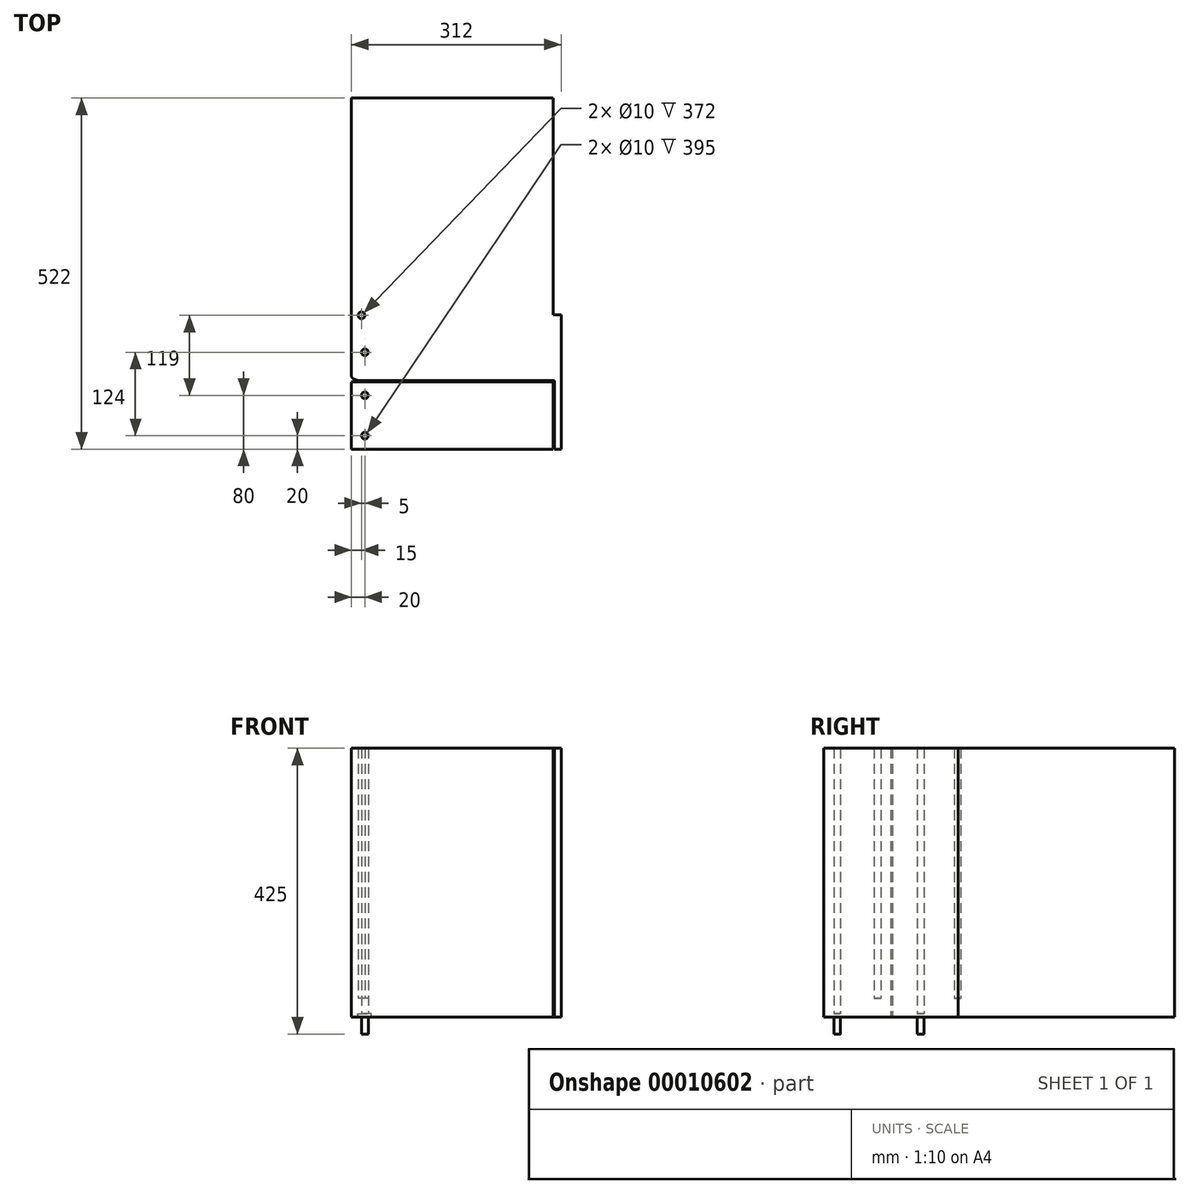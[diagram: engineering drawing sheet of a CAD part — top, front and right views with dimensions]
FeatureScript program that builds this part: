
annotation { "Feature Type Name" : "Feature", "Feature Type Description" : "" }
export const myFeature = defineFeature(function(context is Context, id is Id, definition is map)
    precondition{}
    {
        {
            var Q0;
            Q0=qCreatedBy(makeId("Top.planeOp"),FACE);
            var sketch = newSketch(context, id + "F0", { "sketchPlane" : qUnion([Q0])});
            skLineSegment(sketch, "E0.bottom", {"start": v(0, 420) * mm, "end": v(300, 420) * mm});
            skLineSegment(sketch, "E0.top", {"start": v(0, 0) * mm, "end": v(300, 0) * mm});
            skLineSegment(sketch, "E0.left", {"start": v(0, 420) * mm, "end": v(0, 0) * mm});
            skLineSegment(sketch, "E0.right", {"start": v(300, 420) * mm, "end": v(300, 0) * mm});
            skLineSegment(sketch, "E1.bottom", {"start": v(0, -2) * mm, "end": v(300, -2) * mm});
            skLineSegment(sketch, "E1.top", {"start": v(0, -102) * mm, "end": v(300, -102) * mm});
            skLineSegment(sketch, "E1.left", {"start": v(0, -2) * mm, "end": v(0, -102) * mm});
            skLineSegment(sketch, "E1.right", {"start": v(300, -2) * mm, "end": v(300, -102) * mm});
            skCircle(sketch, "E2", {"center": v(20, 42) * mm, "radius": 5 * mm});
            skCircle(sketch, "E3", {"center": v(15, 97) * mm, "radius": 5 * mm});
            skCircle(sketch, "E4", {"center": v(20, -22) * mm, "radius": 5 * mm});
            skCircle(sketch, "E5", {"center": v(20, -82) * mm, "radius": 5 * mm});
            skLineSegment(sketch, "E6.bottom", {"start": v(-62.26, -84.61) * mm, "end": v(209.63, -211.4) * mm, "construction": true});
            skLineSegment(sketch, "E6.top", {"start": v(-20, 6.02) * mm, "end": v(251.9, -120.77) * mm, "construction": true});
            skLineSegment(sketch, "E6.left", {"start": v(-20, 6.02) * mm, "end": v(-62.26, -84.61) * mm, "construction": true});
            skLineSegment(sketch, "E6.right", {"start": v(251.9, -120.77) * mm, "end": v(209.63, -211.4) * mm, "construction": true});
            skCircle(sketch, "E7", {"center": v(-10.33, -20.56) * mm, "radius": 5 * mm, "construction": true});
            skCircle(sketch, "E8", {"center": v(-35.68, -74.94) * mm, "radius": 5 * mm, "construction": true});
            skLineSegment(sketch, "E9", {"start": v(-35.68, -74.94) * mm, "end": v(20, -82) * mm, "construction": true});
            skLineSegment(sketch, "E10", {"start": v(-7.84, -78.47) * mm, "end": v(55.35, 420) * mm, "construction": true});
            skLineSegment(sketch, "E11", {"start": v(-10.33, -20.56) * mm, "end": v(20, -22) * mm, "construction": true});
            skLineSegment(sketch, "E12", {"start": v(4.84, -21.28) * mm, "end": v(25.75, 420) * mm, "construction": true});
            skLineSegment(sketch, "E13.bottom", {"start": v(302, -102) * mm, "end": v(312, -102) * mm});
            skLineSegment(sketch, "E13.top", {"start": v(302, 98) * mm, "end": v(312, 98) * mm});
            skLineSegment(sketch, "E13.left", {"start": v(302, -102) * mm, "end": v(302, 98) * mm});
            skLineSegment(sketch, "E13.right", {"start": v(312, -102) * mm, "end": v(312, 98) * mm});
            skLineSegment(sketch, "E14.bottom", {"start": v(302, 98) * mm, "end": v(300, 98) * mm});
            skLineSegment(sketch, "E14.top", {"start": v(302, 0) * mm, "end": v(300, 0) * mm});
            skLineSegment(sketch, "E14.left", {"start": v(302, 98) * mm, "end": v(302, 0) * mm});
            skLineSegment(sketch, "E14.right", {"start": v(300, 98) * mm, "end": v(300, 0) * mm});
            skSolve(sketch);
        }
        {
            var Q0;
            Q0 = qSketchRegion(id + "F0", true);
            extrude(context, id + "F1", {"entities" : qUnion([Q0]), "depth" : 400 * mm});
        }
        {
            var Q0;
            Q0=qCreatedBy(makeId("Top.planeOp"),FACE);
            var sketch = newSketch(context, id + "F2", { "sketchPlane" : qUnion([Q0])});
            skLineSegment(sketch, "E15", {"start": v(25, 97.42) * mm, "end": v(30, -21.58) * mm});
            skLineSegment(sketch, "E16", {"start": v(10, -22.42) * mm, "end": v(5, 96.58) * mm});
            skArc(sketch, "E17", {"start": v(5, 96.58) * mm, "mid": v(14.58, 107) * mm, "end": v(25, 97.42) * mm});
            skArc(sketch, "E18", {"start": v(30, -21.58) * mm, "mid": v(20.42, -32) * mm, "end": v(10, -22.42) * mm});
            skCircle(sketch, "E19", {"center": v(15, 97) * mm, "radius": 5 * mm});
            skCircle(sketch, "E20", {"center": v(20, -22) * mm, "radius": 5 * mm});
            skSolve(sketch);
        }
        {
            var Q0;
            {var subQ3=sQuery(id+"F2.wireOp",EDGE,"E16");Q0=makeQuery(id+"F2.imprint","IMPRINT",FACE,{"disambiguationData":[TD([[makeQuery(id+"F2.imprint","IMPRINT",EDGE,{"derivedFrom":subQ3}),-1.0]])]});}
            var Q1;
            {var subQ0=sQuery(id+"F2.wireOp",EDGE,"E18");var subQ1=sQuery(id+"F2.wireOp",EDGE,"1002cabe-0871-408c-8a85-3f84f857aeda");var subQ2=makeQuery(id+"F2.imprint","INTERSECT",VERTEX,{"derivedFrom":[subQ1,subQ0]});Q1=makeQuery(id+"F2.imprint","IMPRINT",FACE,{"disambiguationData":[TD([[makeQuery(id+"F2.imprint","IMPRINT",EDGE,{"disambiguationData":[TD([[subQ2,-1.0]])],"derivedFrom":subQ1}),-1.0]])]});}
            var Q2;
            Q2=makeQuery(id+"F2.imprint","IMPRINT",FACE,{"disambiguationData":[TD([[makeQuery(id+"F2.imprint","IMPRINT",EDGE,{"derivedFrom":sQuery(id+"F2.wireOp",EDGE,"E20")}),1.0]])]});
            var Q3;
            Q3=makeQuery(id+"F2.imprint","IMPRINT",FACE,{"disambiguationData":[TD([[makeQuery(id+"F2.imprint","IMPRINT",EDGE,{"derivedFrom":sQuery(id+"F2.wireOp",EDGE,"E19")}),1.0]])]});
            extrude(context, id + "F3", {"entities" : qUnion([Q0, Q1, Q2, Q3]), "depth" : 5 * mm});
        }
        {
            var Q0;
            Q0=makeQuery(id+"F2.imprint","IMPRINT",FACE,{"disambiguationData":[TD([[makeQuery(id+"F2.imprint","IMPRINT",EDGE,{"derivedFrom":sQuery(id+"F2.wireOp",EDGE,"E19")}),1.0]])]});
            var Q1;
            Q1=makeQuery(id+"F2.imprint","IMPRINT",FACE,{"disambiguationData":[TD([[makeQuery(id+"F2.imprint","IMPRINT",EDGE,{"derivedFrom":sQuery(id+"F2.wireOp",EDGE,"E20")}),1.0]])]});
            extrude(context, id + "F4", {"entities" : qUnion([Q0, Q1]), "operationType" : NewBodyOperationType.ADD, "depth" : 28 * mm});
        }
        {
            var Q0;
            Q0=qCreatedBy(makeId("Top.planeOp"),FACE);
            var sketch = newSketch(context, id + "F5", { "sketchPlane" : qUnion([Q0])});
            skLineSegment(sketch, "E21", {"start": v(30, 42) * mm, "end": v(30, -82) * mm});
            skLineSegment(sketch, "E22", {"start": v(10, -82) * mm, "end": v(10, 42) * mm});
            skArc(sketch, "E23", {"start": v(10, 42) * mm, "mid": v(20, 52) * mm, "end": v(30, 42) * mm});
            skArc(sketch, "E24", {"start": v(30, -82) * mm, "mid": v(20, -92) * mm, "end": v(10, -82) * mm});
            skCircle(sketch, "E25", {"center": v(20, 42) * mm, "radius": 5 * mm});
            skCircle(sketch, "E26", {"center": v(20, -82) * mm, "radius": 5 * mm});
            skSolve(sketch);
        }
        {
            var Q0;
            Q0=makeQuery(id+"F5.imprint","IMPRINT",FACE,{"disambiguationData":[TD([[makeQuery(id+"F5.imprint","IMPRINT",EDGE,{"derivedFrom":sQuery(id+"F5.wireOp",EDGE,"E21")}),-1.0]])]});
            var Q1;
            Q1=makeQuery(id+"F5.imprint","IMPRINT",FACE,{"disambiguationData":[TD([[makeQuery(id+"F5.imprint","IMPRINT",EDGE,{"derivedFrom":sQuery(id+"F5.wireOp",EDGE,"E25")}),1.0]])]});
            var Q2;
            Q2=makeQuery(id+"F5.imprint","IMPRINT",FACE,{"disambiguationData":[TD([[makeQuery(id+"F5.imprint","IMPRINT",EDGE,{"derivedFrom":sQuery(id+"F5.wireOp",EDGE,"E26")}),1.0]])]});
            extrude(context, id + "F6", {"entities" : qUnion([Q0, Q1, Q2]), "depth" : 5 * mm});
        }
        {
            var Q0;
            Q0=makeQuery(id+"F5.imprint","IMPRINT",FACE,{"disambiguationData":[TD([[makeQuery(id+"F5.imprint","IMPRINT",EDGE,{"derivedFrom":sQuery(id+"F5.wireOp",EDGE,"E26")}),1.0]])]});
            var Q1;
            Q1=makeQuery(id+"F5.imprint","IMPRINT",FACE,{"disambiguationData":[TD([[makeQuery(id+"F5.imprint","IMPRINT",EDGE,{"derivedFrom":sQuery(id+"F5.wireOp",EDGE,"E25")}),1.0]])]});
            var Q2;
            Q2=sQuery(id+"F2.wireOp",EDGE,"E19");
            var Q3;
            Q3=sQuery(id+"F2.wireOp",EDGE,"E20");
            extrude(context, id + "F7", {"entities" : qUnion([Q0, Q1]), "operationType" : NewBodyOperationType.ADD, "surfaceEntities" : qUnion([Q2, Q3]), "oppositeDirection" : true, "depth" : 25 * mm});
        }
        {
            var Q0;
            Q0=makeQuery(id+"F1.opExtrude","SWEPT_EDGE",EDGE,{"disambiguationData":[OSD([sQuery(id+"F0.wireOp",EDGE,"E0.top"),sQuery(id+"F0.wireOp",EDGE,"E0.left")])]});
            chamfer(context, id + "F8", {"entities" : qUnion([Q0]), "chamferType" : ChamferType.TWO_OFFSETS, "width1" : 9 * mm, "oppositeDirection" : false, "width2" : 4 * mm});
        }
        {
            var Q0;
            Q0=makeQuery(id+"F1.opExtrude","SWEPT_EDGE",EDGE,{"disambiguationData":[OSD([sQuery(id+"F0.wireOp",EDGE,"E0.top"),sQuery(id+"F0.wireOp",EDGE,"E0.left")])]});
            var Q1;
            {var subQ0=sQuery(id+"F0.wireOp",EDGE,"E0.left");Q1=makeQuery(id+"F8.opChamfer","BLEND_EDGE",EDGE,{"blendedFrom":[makeQuery(id+"F1.opExtrude","SWEPT_EDGE",EDGE,{"disambiguationData":[OSD([sQuery(id+"F0.wireOp",EDGE,"E0.top"),subQ0])]}),makeQuery(id+"F1.opExtrude","SWEPT_FACE",FACE,{"disambiguationData":[OSD([subQ0])]})],"blendedInto":[makeQuery(id+"F1.opExtrude","SWEPT_FACE",FACE,{"disambiguationData":[OSD([subQ0])]})]});}
            var Q2;
            {var subQ0=sQuery(id+"F0.wireOp",EDGE,"E0.top");Q2=makeQuery(id+"F8.opChamfer","BLEND_EDGE",EDGE,{"blendedFrom":[makeQuery(id+"F1.opExtrude","SWEPT_EDGE",EDGE,{"disambiguationData":[OSD([subQ0,sQuery(id+"F0.wireOp",EDGE,"E0.left")])]}),makeQuery(id+"F1.opExtrude","SWEPT_FACE",FACE,{"disambiguationData":[OSD([subQ0,sQuery(id+"F0.wireOp",EDGE,"E14.top")])]})],"blendedInto":[makeQuery(id+"F1.opExtrude","SWEPT_FACE",FACE,{"disambiguationData":[OSD([subQ0,sQuery(id+"F0.wireOp",EDGE,"E14.top")])]})]});}
            fillet(context, id + "F9", {"entities" : qUnion([Q0, Q1, Q2]), "radius" : 5 * mm, "allowEdgeOverflow" : false});
        }
    });
